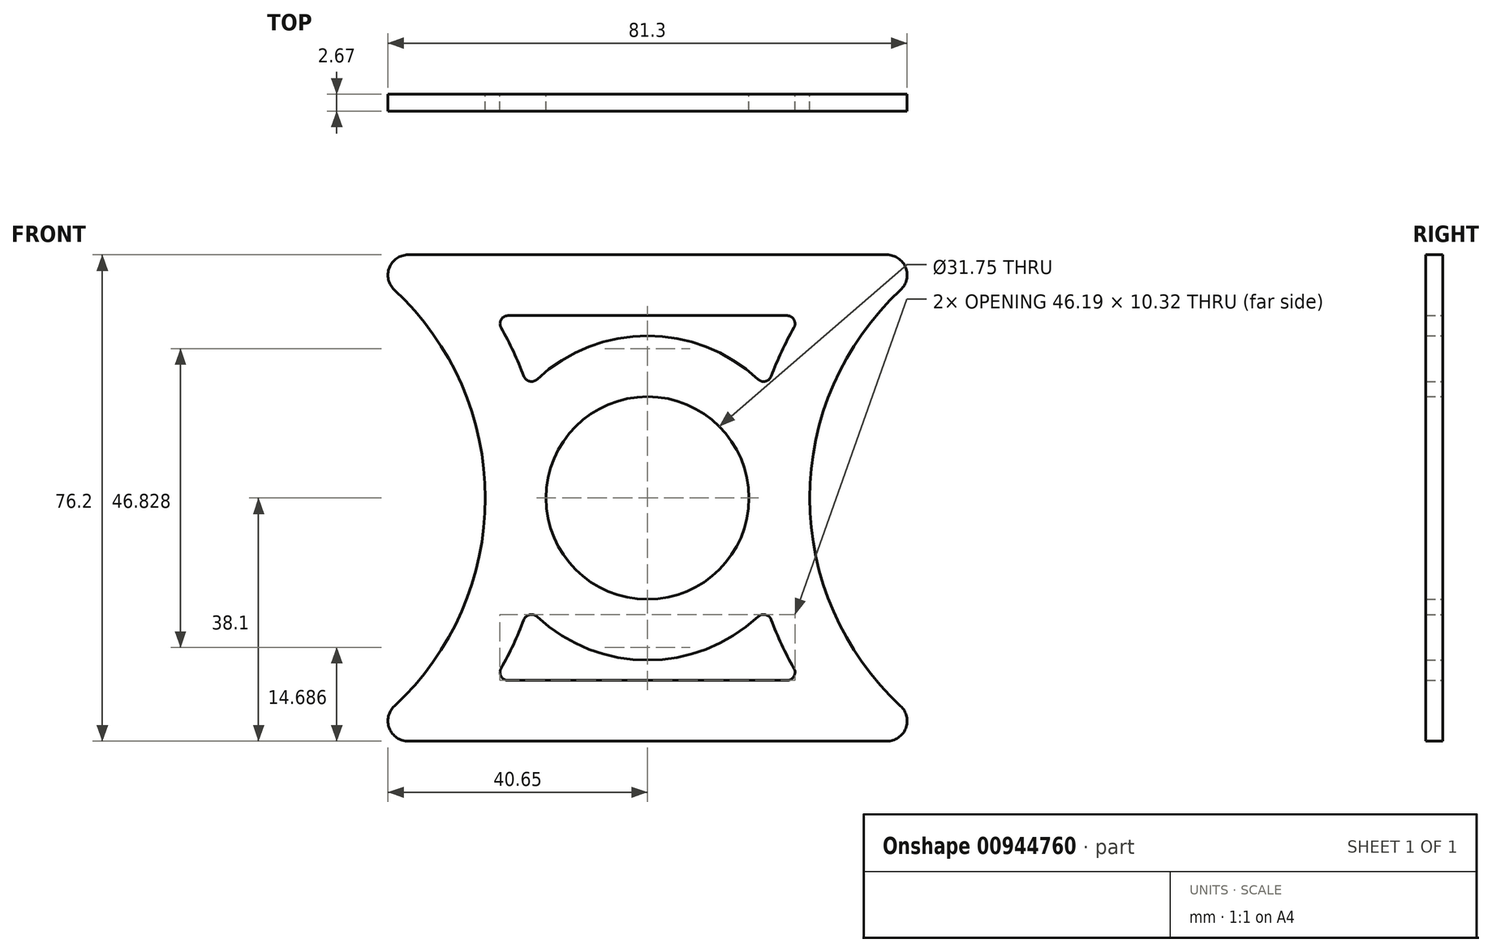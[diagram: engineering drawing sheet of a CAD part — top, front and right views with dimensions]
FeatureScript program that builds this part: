
annotation { "Feature Type Name" : "Feature", "Feature Type Description" : "" }
export const myFeature = defineFeature(function(context is Context, id is Id, definition is map)
    precondition{}
    {
        {
            var Q0;
            Q0=qCreatedBy(makeId("Front.planeOp"),FACE);
            var sketch = newSketch(context, id + "F0", { "sketchPlane" : qUnion([Q0])});
            skLineSegment(sketch, "E0.bottom", {"start": v(-107.32, 38.1) * mm, "end": v(-32.38, 38.1) * mm});
            skLineSegment(sketch, "E0.top", {"start": v(-107.32, -38.1) * mm, "end": v(-32.38, -38.1) * mm});
            skArc(sketch, "E1", {"start": v(-109.48, -32.6) * mm, "mid": v(-95.25, 0) * mm, "end": v(-109.48, 32.6) * mm});
            skArc(sketch, "E2", {"start": v(-30.22, 32.6) * mm, "mid": v(-44.45, 0) * mm, "end": v(-30.22, -32.6) * mm});
            skArc(sketch, "E3", {"start": v(-107.32, 38.1) * mm, "mid": v(-110.28, 36.08) * mm, "end": v(-109.48, 32.6) * mm});
            skArc(sketch, "E4", {"start": v(-109.48, -32.6) * mm, "mid": v(-110.28, -36.08) * mm, "end": v(-107.32, -38.1) * mm});
            skArc(sketch, "E5", {"start": v(-30.22, 32.6) * mm, "mid": v(-29.42, 36.08) * mm, "end": v(-32.38, 38.1) * mm});
            skArc(sketch, "E6", {"start": v(-32.38, -38.1) * mm, "mid": v(-29.42, -36.08) * mm, "end": v(-30.22, -32.6) * mm});
            skCircle(sketch, "E7", {"center": v(-69.85, 0) * mm, "radius": 15.87 * mm});
            skLineSegment(sketch, "E8", {"start": v(-69.85, 38.1) * mm, "end": v(-69.85, -38.1) * mm, "construction": true});
            skLineSegment(sketch, "E9", {"start": v(-91.67, 28.58) * mm, "end": v(-48.03, 28.58) * mm});
            skArc(sketch, "E10", {"start": v(-52.55, 18.6) * mm, "mid": v(-69.85, 25.4) * mm, "end": v(-87.15, 18.6) * mm});
            skArc(sketch, "E11", {"start": v(-89.2, 19.07) * mm, "mid": v(-90.85, 22.95) * mm, "end": v(-92.78, 26.68) * mm});
            skArc(sketch, "E12", {"start": v(-46.92, 26.68) * mm, "mid": v(-48.85, 22.95) * mm, "end": v(-50.5, 19.07) * mm});
            skPoint(sketch, "E13.visualSharp", {"position": v(-88.54, 17.2) * mm});
            skArc(sketch, "E13.filletArc", {"start": v(-89.2, 19.07) * mm, "mid": v(-88.3, 18.29) * mm, "end": v(-87.15, 18.6) * mm});
            skPoint(sketch, "E14.visualSharp", {"position": v(-51.16, 17.2) * mm});
            skArc(sketch, "E14.filletArc", {"start": v(-52.55, 18.6) * mm, "mid": v(-51.4, 18.29) * mm, "end": v(-50.5, 19.07) * mm});
            skPoint(sketch, "E15.visualSharp", {"position": v(-45.8, 28.58) * mm});
            skArc(sketch, "E15.filletArc", {"start": v(-46.92, 26.68) * mm, "mid": v(-46.93, 27.94) * mm, "end": v(-48.03, 28.58) * mm});
            skPoint(sketch, "E16.visualSharp", {"position": v(-93.9, 28.58) * mm});
            skArc(sketch, "E16.filletArc", {"start": v(-91.67, 28.58) * mm, "mid": v(-92.77, 27.94) * mm, "end": v(-92.78, 26.68) * mm});
            skLineSegment(sketch, "E17", {"start": v(-130.62, 0) * mm, "end": v(0, 0) * mm, "construction": true});
            skArc(sketch, "E18.MirrorCS", {"start": v(-52.55, -18.6) * mm, "mid": v(-51.4, -18.29) * mm, "end": v(-50.5, -19.07) * mm});
            skArc(sketch, "E19.MirrorCS", {"start": v(-89.2, -19.07) * mm, "mid": v(-88.3, -18.29) * mm, "end": v(-87.15, -18.6) * mm});
            skArc(sketch, "E20.MirrorCS", {"start": v(-46.92, -26.68) * mm, "mid": v(-46.93, -27.94) * mm, "end": v(-48.03, -28.58) * mm});
            skArc(sketch, "E21.MirrorCS", {"start": v(-91.67, -28.58) * mm, "mid": v(-92.77, -27.94) * mm, "end": v(-92.78, -26.68) * mm});
            skArc(sketch, "E22.MirrorCS", {"start": v(-89.2, -19.07) * mm, "mid": v(-90.85, -22.95) * mm, "end": v(-92.78, -26.68) * mm});
            skLineSegment(sketch, "E23.MirrorCS", {"start": v(-91.67, -28.58) * mm, "end": v(-48.03, -28.58) * mm});
            skPoint(sketch, "E24.MirrorP", {"position": v(-45.8, -28.58) * mm});
            skPoint(sketch, "E25.MirrorP", {"position": v(-88.54, -17.2) * mm});
            skArc(sketch, "E26.MirrorCS", {"start": v(-52.55, -18.6) * mm, "mid": v(-69.85, -25.4) * mm, "end": v(-87.15, -18.6) * mm});
            skArc(sketch, "E27.MirrorCS", {"start": v(-46.92, -26.68) * mm, "mid": v(-48.85, -22.95) * mm, "end": v(-50.5, -19.07) * mm});
            skPoint(sketch, "E28.MirrorP", {"position": v(-51.16, -17.2) * mm});
            skPoint(sketch, "E29.MirrorP", {"position": v(-93.9, -28.58) * mm});
            skLineSegment(sketch, "E30.MirrorCS", {"start": v(-69.85, -38.1) * mm, "end": v(-69.85, 38.1) * mm, "construction": true});
            skSolve(sketch);
        }
        {
            var Q0;
            Q0=makeQuery(id+"F0.imprint","IMPRINT",FACE,{"disambiguationData":[TD([[makeQuery(id+"F0.imprint","IMPRINT",EDGE,{"derivedFrom":sQuery(id+"F0.wireOp",EDGE,"E0.bottom")}),-1.0]])]});
            extrude(context, id + "F1", {"entities" : qUnion([Q0]), "depth" : 2.67 * mm, "offsetDistance" : 25.4 * mm});
        }
    });
